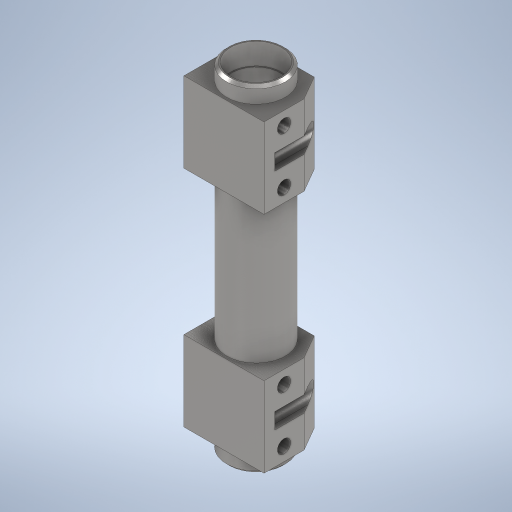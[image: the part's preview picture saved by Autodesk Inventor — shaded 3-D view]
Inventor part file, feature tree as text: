
AUTODESK INVENTOR PART (.ipt)
format: ipt  version: 2024 (Build 280153000, 153)  size: 389,120 bytes
history: native  units: mm
features: sketch x7, plane x4, chamfer x4, hole x4, extrude x3, mirror x3, projected_geometry x1
ambient origin geometry x8: Origin, YZ Plane, XZ Plane, XY Plane, X Axis, Y Axis, Z Axis, Center Point
bodies: Volumenkörper1 (feature_tree)
feature tree (26):
  extrude  "Extrusion1"  Depth=126.0mm TaperAngle=0.0deg
  plane  "Arbeitsebene1"
  extrude  "Extrusion2"  Depth=24.0mm
  chamfer  "Fasen1"  Distance=30.0mm
  chamfer  "Fasen2"  Distance=9.0mm Angle=30.0deg
  plane  "Arbeitsebene2"
  mirror  "Spiegeln1"
  plane  "Arbeitsebene4"
  extrude  "Extrusion3"  [1 undecoded]
  mirror  "Spiegeln2"
  plane  "Arbeitsebene5"
  mirror  "Spiegeln3"
  hole  "Bohrung1"  [1 undecoded]
  hole  "Bohrung2"  [1 undecoded]
  hole  "Bohrung3"  [1 undecoded]
  hole  "Bohrung4"  [1 undecoded]
  chamfer  "Fasen3"  Distance=1.0mm Angle=30.0deg
  chamfer  "Fasen4"  Distance=1.0mm Angle=30.0deg
  sketch  "Skizze1"  dims[d0=22.0mm d1=126.0mm d2=0.0mm]
  sketch  "Skizze2"  dims[d3=-6.0mm d4=24.0mm]
  sketch  "Skizze4"  dims[d5=30.0mm d6=30.0mm d7=0.0mm d8=9.0mm d9=2.0mm d10=30.0deg]
  projected_geometry  "Projizierte Kontur2"
  sketch  "Skizze5"  dims[d11=9.0mm d12=2.0mm d13=30.0deg d14=-63.0mm]
  sketch  "Skizze6"  dims[d17=-31.415927mm d18=2.0mm]
  sketch  "Skizze7"  dims[d19=6.0mm d20=20.0mm d21=0.0mm]
  sketch  "Skizze8"  dims[d22=0.0mm d23=2.0mm d24=6.0mm d25=4.0mm d26=2.0mm d27=90.0deg d28=2.0mm d29=0.0mm d30=5.0mm d31=5.0mm d32=5.0mm d33=6.0mm d34=4.0mm d35=2.0mm d36=90.0deg d37=2.0mm d38=0.0mm d39=19.0mm d40=6.0mm d41=4.0mm d42=2.0mm d43=90.0deg d44=8.0mm d45=0.0mm d46=18.0mm d47=6.0mm d48=4.0mm d49=2.0mm d50=90.0deg d51=8.0mm d52=0.0mm d53=1.0mm d54=2.0mm d55=30.0deg d56=1.0mm d57=2.0mm d58=30.0deg]
note: 5 required parameter values undecoded (feature->parameter linkage not recoverable at this tier; creation-order binding heuristic only, values carry confidence <= 0.55)
